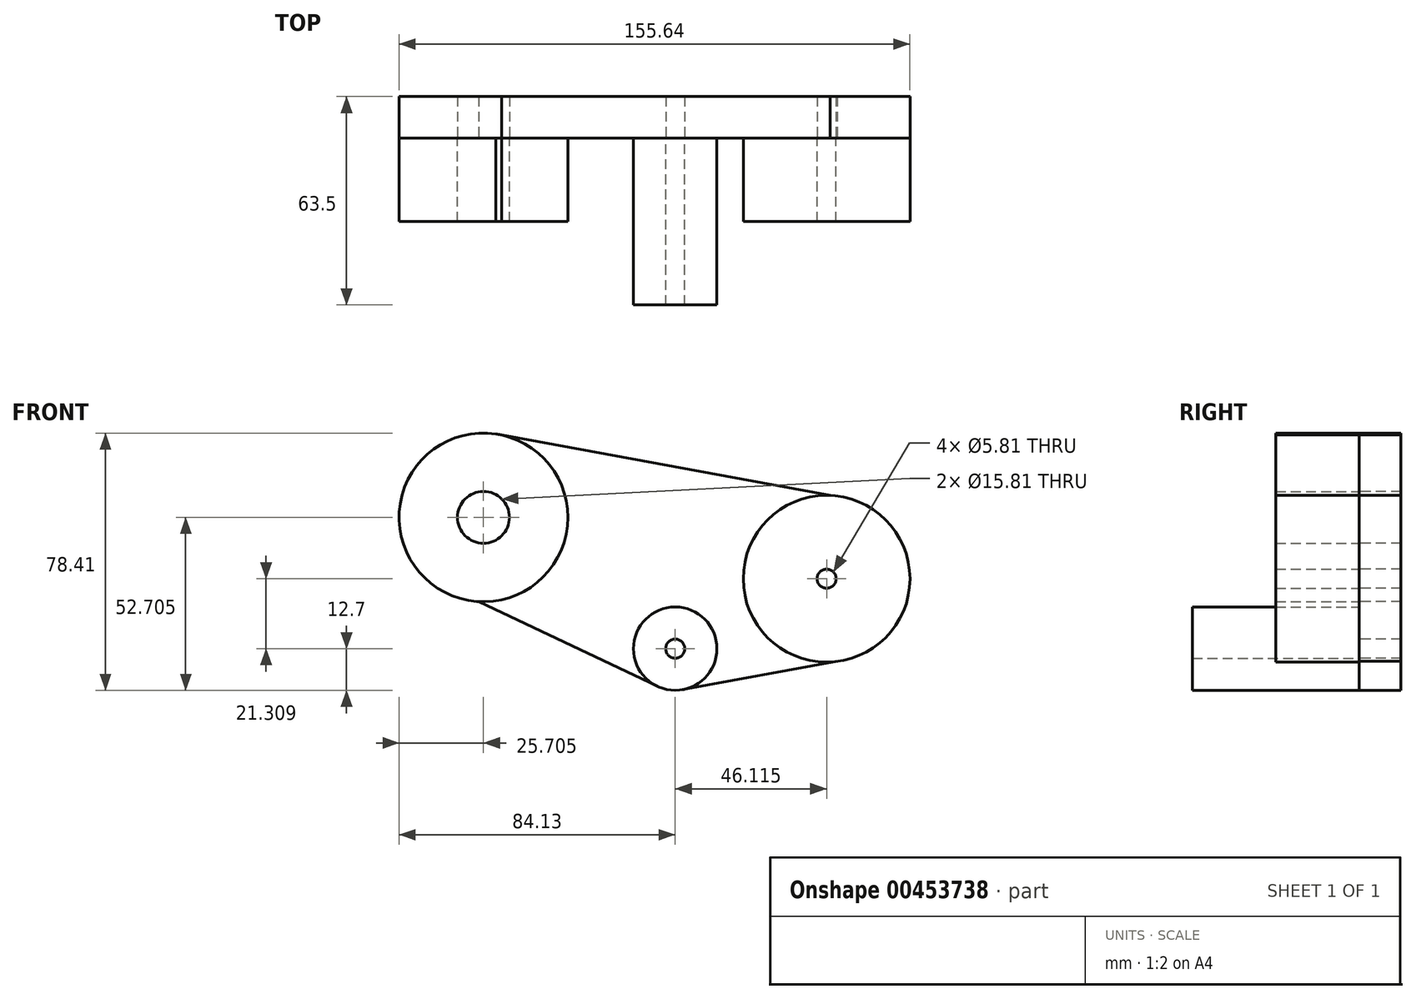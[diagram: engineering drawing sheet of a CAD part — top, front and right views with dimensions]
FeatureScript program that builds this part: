
annotation { "Feature Type Name" : "Feature", "Feature Type Description" : "" }
export const myFeature = defineFeature(function(context is Context, id is Id, definition is map)
    precondition{}
    {
        {
            var Q0;
            Q0=qCreatedBy(makeId("Front.planeOp"),FACE);
            var sketch = newSketch(context, id + "F0", { "sketchPlane" : qUnion([Q0])});
            skCircle(sketch, "E0", {"center": v(0, 0) * mm, "radius": 12.7 * mm});
            skCircle(sketch, "E1", {"center": v(46.11, 21.3) * mm, "radius": 25.4 * mm});
            skCircle(sketch, "E2", {"center": v(0, 0) * mm, "radius": 2.9 * mm});
            skCircle(sketch, "E3", {"center": v(46.11, 21.3) * mm, "radius": 2.9 * mm});
            skCircle(sketch, "E4", {"center": v(-58.42, 40) * mm, "radius": 25.7 * mm});
            skCircle(sketch, "E5", {"center": v(-58.42, 40) * mm, "radius": 7.9 * mm});
            skLineSegment(sketch, "E6", {"start": v(-54.63, 65.43) * mm, "end": v(47.2, 46.69) * mm});
            skLineSegment(sketch, "E7", {"start": v(-59.84, 14.34) * mm, "end": v(-5.44, -11.47) * mm});
            skLineSegment(sketch, "E8", {"start": v(49.4, -3.88) * mm, "end": v(2.28, -12.5) * mm});
            skSolve(sketch);
        }
        {
            var Q0;
            Q0=makeQuery(id+"F0.imprint","IMPRINT",FACE,{"disambiguationData":[TD([[makeQuery(id+"F0.imprint","IMPRINT",EDGE,{"derivedFrom":sQuery(id+"F0.wireOp",EDGE,"E0")}),1.0]])]});
            extrude(context, id + "F1", {"entities" : qUnion([Q0]), "depth" : 50.8 * mm});
        }
        {
            var Q0;
            Q0=makeQuery(id+"F0.imprint","IMPRINT",FACE,{"disambiguationData":[TD([[makeQuery(id+"F0.imprint","IMPRINT",EDGE,{"derivedFrom":sQuery(id+"F0.wireOp",EDGE,"E1")}),1.0]])]});
            extrude(context, id + "F2", {"entities" : qUnion([Q0]), "depth" : 25.4 * mm});
        }
        {
            var Q0;
            Q0=makeQuery(id+"F0.imprint","IMPRINT",FACE,{"disambiguationData":[TD([[makeQuery(id+"F0.imprint","IMPRINT",EDGE,{"derivedFrom":sQuery(id+"F0.wireOp",EDGE,"E5")}),-1.0]])]});
            extrude(context, id + "F3", {"entities" : qUnion([Q0]), "depth" : 25.4 * mm});
        }
        {
            var Q0;
            Q0 = qSketchRegion(id + "F0", true);
            extrude(context, id + "F4", {"entities" : qUnion([Q0]), "oppositeDirection" : true, "depth" : 12.7 * mm});
        }
    });
